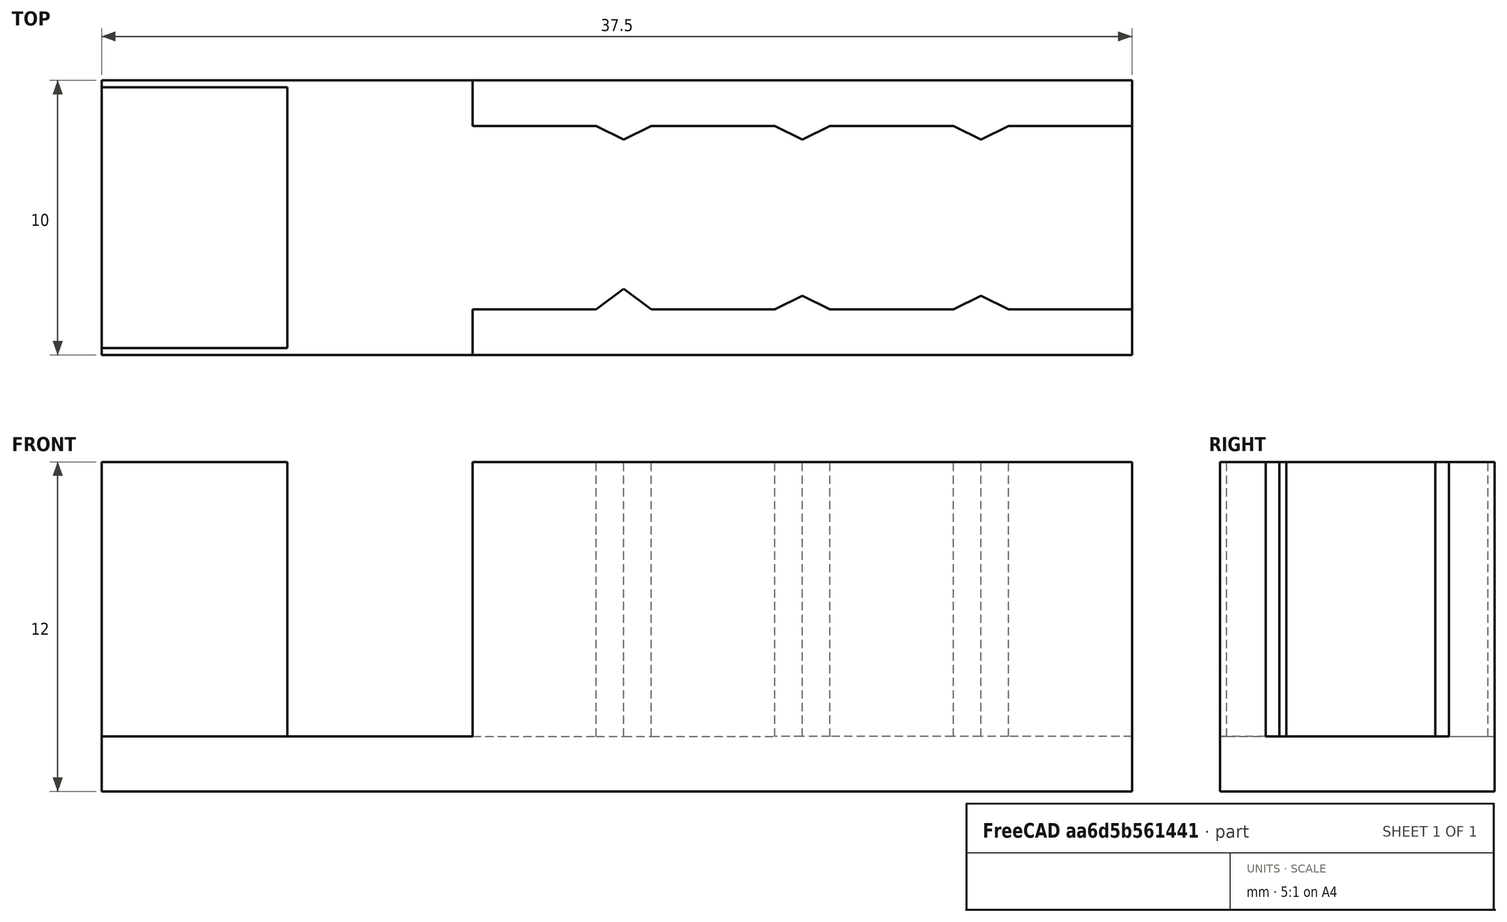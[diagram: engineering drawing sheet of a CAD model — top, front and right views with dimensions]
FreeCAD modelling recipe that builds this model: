
FCSTD DOCUMENT  (FreeCAD 0.20R29177 +426 (Git))
Label: shower_door_edge_adjuster_6mm
License: Creative Commons Attribution
LicenseURL: http://creativecommons.org/licenses/by/3.0/
objects: Sketcher::SketchObject×2, PartDesign::Pad×2, PartDesign::Body×1, Mesh::Feature×1
note: 7 computed .brp shape members not serialized (recipe doc carries the construction recipe); baked Part::Feature solids carry a one-line shape summary decoded from their .brp

FEATURE [Sketcher::SketchObject] Sketch
  FullyConstrained = true
  MapMode = 5
  Support = -> [XY_Plane]
  sketch-geometry (6):
    g0: LineSegment StartX=0 StartY=-5 StartZ=0 EndX=4.32391e-11 EndY=5 EndZ=0
    g1: LineSegment StartX=13.5 StartY=5 StartZ=0 EndX=37.5 EndY=5 EndZ=0
    g2: LineSegment StartX=37.5 StartY=5 StartZ=0 EndX=37.5 EndY=-5 EndZ=0
    g3: LineSegment StartX=37.5 StartY=-5 StartZ=0 EndX=13.5 EndY=-5 EndZ=0
    g4: LineSegment StartX=13.5 StartY=-5 StartZ=0 EndX=0 EndY=-5 EndZ=0
    g5: LineSegment StartX=0 StartY=5 StartZ=0 EndX=13.5 EndY=5 EndZ=0
  constraints (17):
    c: PointOnObject(g0,g-2)
    c: Horizontal(g1)
    c: Coincident(g1,g2)
    c: Coincident(g2,g3)
    c: Horizontal(g3)
    c: Coincident(g4,g0)
    c: Horizontal(g4)
    c: DistanceY(g0,g0) = 10  'DoorThickness'
    c: Symmetric(g0,g0,g-1)
    c: Symmetric(g1,g2,g-1)
    c: DistanceX(g1,g1) = 24  'GripLength'
    c: Equal(g1,g3)
    c: PointOnObject(g5,g0)
    c: Coincident(g5,g1)
    c: Horizontal(g5)
    c: Coincident(g3,g4)
    c: DistanceX(g5,g5) = 13.5  'PocketDepth'
FEATURE [PartDesign::Pad] Pad
  Direction = (0,0,1)
  Length = 2
  Length2 = 10
  Profile = -> Sketch
  ReferenceAxis = -> Sketch [N_Axis]
  Type = 0
FEATURE [Sketcher::SketchObject] Sketch003  label="Sketch002"
  FullyConstrained = true
  MapMode = 5
  Placement = pos=(0,0,2) rot=(0,0,1;0rad)
  Support = -> [Pad]
  expr: .Constraints.GripLength = 24mm
  expr: .Constraints.GripThickness = 2.16
  expr: .Constraints.GripWall = .Constraints.GripThickness - 0.5mm
  expr: Constraints[10] = Sketch.Constraints.PocketDepth / 2
  expr: Constraints[53] = Sketch.Constraints.PocketDepth
  expr: Constraints[54] = Sketch.Constraints.DoorThickness
  expr: Constraints[57] = .Constraints.GripThickness
  expr: Constraints[58] = .Constraints.GripThickness
  expr: Constraints[59] = .Constraints.GripThickness
  expr: Constraints[60] = .Constraints.GripThickness
  expr: Constraints[64] = .Constraints.GripWall
  expr: Constraints[65] = .Constraints.GripWall
  expr: Constraints[66] = .Constraints.GripWall
  expr: Constraints[67] = .Constraints.GripWall
  expr: Constraints[68] = (.Constraints.GripLength - 6mm) / 4
  expr: Constraints[77] = .Constraints.GripFinger
  expr: Constraints[78] = .Constraints.GripFinger
  expr: Constraints[79] = .Constraints.GripFinger
  expr: Constraints[85] = .Constraints.GripThickness
  expr: Constraints[9] = Sketch.Constraints.DoorThickness - 0.5mm
  sketch-geometry (31):
    g0: LineSegment StartX=6.75 StartY=-4.75 StartZ=0 EndX=6.75 EndY=4.75 EndZ=0
    g1: LineSegment StartX=6.75 StartY=4.75 StartZ=0 EndX=0 EndY=4.75 EndZ=0
    g2: LineSegment StartX=0 StartY=4.75 StartZ=0 EndX=0 EndY=-4.75 EndZ=0
    g3: LineSegment StartX=0 StartY=-4.75 StartZ=0 EndX=6.75 EndY=-4.75 EndZ=0
    g4: GeomPoint X=3.375 Y=2e-16 Z=0
    g5: LineSegment StartX=13.5 StartY=5 StartZ=0 EndX=37.5 EndY=5 EndZ=0
    g6: LineSegment StartX=37.5 StartY=5 StartZ=0 EndX=37.5 EndY=3.34 EndZ=0
    g7: LineSegment StartX=37.5 StartY=3.34 StartZ=0 EndX=33 EndY=3.34 EndZ=0
    g8: LineSegment StartX=33 StartY=3.34 StartZ=0 EndX=32 EndY=2.84 EndZ=0
    g9: LineSegment StartX=32 StartY=2.84 StartZ=0 EndX=31 EndY=3.34 EndZ=0
    g10: LineSegment StartX=31 StartY=3.34 StartZ=0 EndX=26.5 EndY=3.34 EndZ=0
    g11: LineSegment StartX=26.5 StartY=3.34 StartZ=0 EndX=25.5 EndY=2.84 EndZ=0
    g12: LineSegment StartX=25.5 StartY=2.84 StartZ=0 EndX=24.5 EndY=3.34 EndZ=0
    g13: LineSegment StartX=13.5 StartY=3.34 StartZ=0 EndX=13.5 EndY=5 EndZ=0
    g14: LineSegment StartX=24.5 StartY=3.34 StartZ=0 EndX=20 EndY=3.34 EndZ=0
    g15: LineSegment StartX=20 StartY=3.34 StartZ=0 EndX=19 EndY=2.84 EndZ=0
    g16: LineSegment StartX=19 StartY=2.84 StartZ=0 EndX=18 EndY=3.34 EndZ=0
    g17: LineSegment StartX=18 StartY=3.34 StartZ=0 EndX=13.5 EndY=3.34 EndZ=0
    g18: LineSegment StartX=13.5 StartY=-5 StartZ=0 EndX=37.5 EndY=-5 EndZ=0
    g19: LineSegment StartX=37.5 StartY=-5 StartZ=0 EndX=37.5 EndY=-3.34 EndZ=0
    g20: LineSegment StartX=37.5 StartY=-3.34 StartZ=0 EndX=33 EndY=-3.34 EndZ=0
    g21: LineSegment StartX=33 StartY=-3.34 StartZ=0 EndX=32 EndY=-2.84 EndZ=0
    g22: LineSegment StartX=32 StartY=-2.84 StartZ=0 EndX=31 EndY=-3.34 EndZ=0
    g23: LineSegment StartX=31 StartY=-3.34 StartZ=0 EndX=26.5 EndY=-3.34 EndZ=0
    g24: LineSegment StartX=26.5 StartY=-3.34 StartZ=0 EndX=25.5 EndY=-2.84 EndZ=0
    g25: LineSegment StartX=25.5 StartY=-2.84 StartZ=0 EndX=24.5 EndY=-3.34 EndZ=0
    g26: LineSegment StartX=13.5 StartY=-3.34 StartZ=0 EndX=13.5 EndY=-5 EndZ=0
    g27: LineSegment StartX=13.5 StartY=-3.34 StartZ=0 EndX=18 EndY=-3.34 EndZ=0
    g28: LineSegment StartX=19 StartY=-2.59 StartZ=0 EndX=20 EndY=-3.34 EndZ=0
    g29: LineSegment StartX=20 StartY=-3.34 StartZ=0 EndX=24.5 EndY=-3.34 EndZ=0
    g30: LineSegment StartX=18 StartY=-3.34 StartZ=0 EndX=19 EndY=-2.59 EndZ=0
  constraints (89):
    c: Coincident(g0,g1)
    c: Coincident(g1,g2)
    c: Coincident(g2,g3)
    c: Coincident(g3,g0)
    c: Horizontal(g1)
    c: Horizontal(g3)
    c: Vertical(g2)
    c: Symmetric(g1,g0,g4)
    c: Symmetric(g0,g0,g-1)
    c: DistanceY(g2,g1) = 9.5
    c: DistanceX(g2,g0) = 6.75
    c: DistanceX(g1) = 0
    c: Horizontal(g5)
    c: Coincident(g5,g6)
    c: Coincident(g6,g7)
    c: Coincident(g7,g8)
    c: Coincident(g8,g9)
    c: Coincident(g9,g10)
    c: Horizontal(g10)
    c: Coincident(g10,g11)
    c: Coincident(g11,g12)
    c: Coincident(g13,g5)
    c: Coincident(g12,g14)
    c: Horizontal(g14)
    c: Coincident(g14,g15)
    c: Coincident(g15,g16)
    c: Coincident(g16,g17)
    c: Coincident(g17,g13)
    c: Vertical(g13)
    c: Vertical(g6)
    c: DistanceY(g15,g5) = 2.16  'GripThickness'
    c: Horizontal(g18)
    c: Coincident(g18,g19)
    c: Vertical(g19)
    c: Coincident(g19,g20)
    c: Horizontal(g20)
    c: Coincident(g20,g21)
    c: Coincident(g21,g22)
    c: Coincident(g22,g23)
    c: Horizontal(g23)
    c: Coincident(g23,g24)
    c: Coincident(g24,g25)
    c: Coincident(g26,g18)
    c: Coincident(g26,g27)
    c: Horizontal(g27)
    c: Coincident(g28,g29)
    c: Coincident(g29,g25)
    c: Horizontal(g29)
    c: Symmetric(g18,g5,g-1)
    c: Vertical(g26)
    c: Equal(g13,g26)
    c: DistanceX(g5,g5) = 24  'GripLength'
    c: Equal(g18,g5)
    c: DistanceX(g1,g5) = 13.5
    c: DistanceY(g18,g5) = 10
    c: Horizontal(g17)
    c: Horizontal(g7)
    c: DistanceY(g11,g5) = 2.16
    c: DistanceY(g8,g5) = 2.16
    c: DistanceY(g18,g24) = 2.16
    c: DistanceY(g18,g21) = 2.16
    c: DistanceY(g26,g26) = 1.66  'GripWall'
    c: Equal(g13,g6)
    c: Equal(g6,g19)
    c: DistanceY(g14,g5) = 1.66
    c: DistanceY(g10,g5) = 1.66
    c: DistanceY(g18,g28) = 1.66
    c: DistanceY(g18,g23) = 1.66
    c: DistanceX(g17,g17) = 4.5
    c: Equal(g14,g10)
    c: Equal(g10,g7)
    c: Equal(g7,g27)
    c: Equal(g27,g29)
    c: Equal(g29,g23)
    c: Equal(g23,g20)
    c: Equal(g20,g17)
    c: DistanceX(g16,g14) = 2  'GripFinger'
    c: DistanceX(g12,g10) = 2
    c: DistanceX(g27,g28) = 2
    c: DistanceX(g22,g20) = 2
    c: Equal(g21,g22)
    c: Equal(g22,g24)
    c: Equal(g22,g9)
    c: Equal(g9,g12)
    c: Equal(g12,g16)
    c: DistanceY(g2,g28) = 2.16
    c: Coincident(g28,g30)
    c: Coincident(g30,g27)
    c: Equal(g30,g28)
FEATURE [PartDesign::Pad] Pad001
  BaseFeature = -> Pad
  Direction = (0,0,1)
  Length = 10
  Length2 = 10
  Profile = -> Sketch003
  ReferenceAxis = -> Sketch003 [N_Axis]
  Type = 0
FEATURE [PartDesign::Body] Body
  Group = -> [Sketch,Pad,Sketch003,Pad001]
  Origin = -> Origin
  Tip = -> Pad001
FEATURE [Mesh::Feature] Mesh  label="shower_door_edge_adjuster_6mm"
